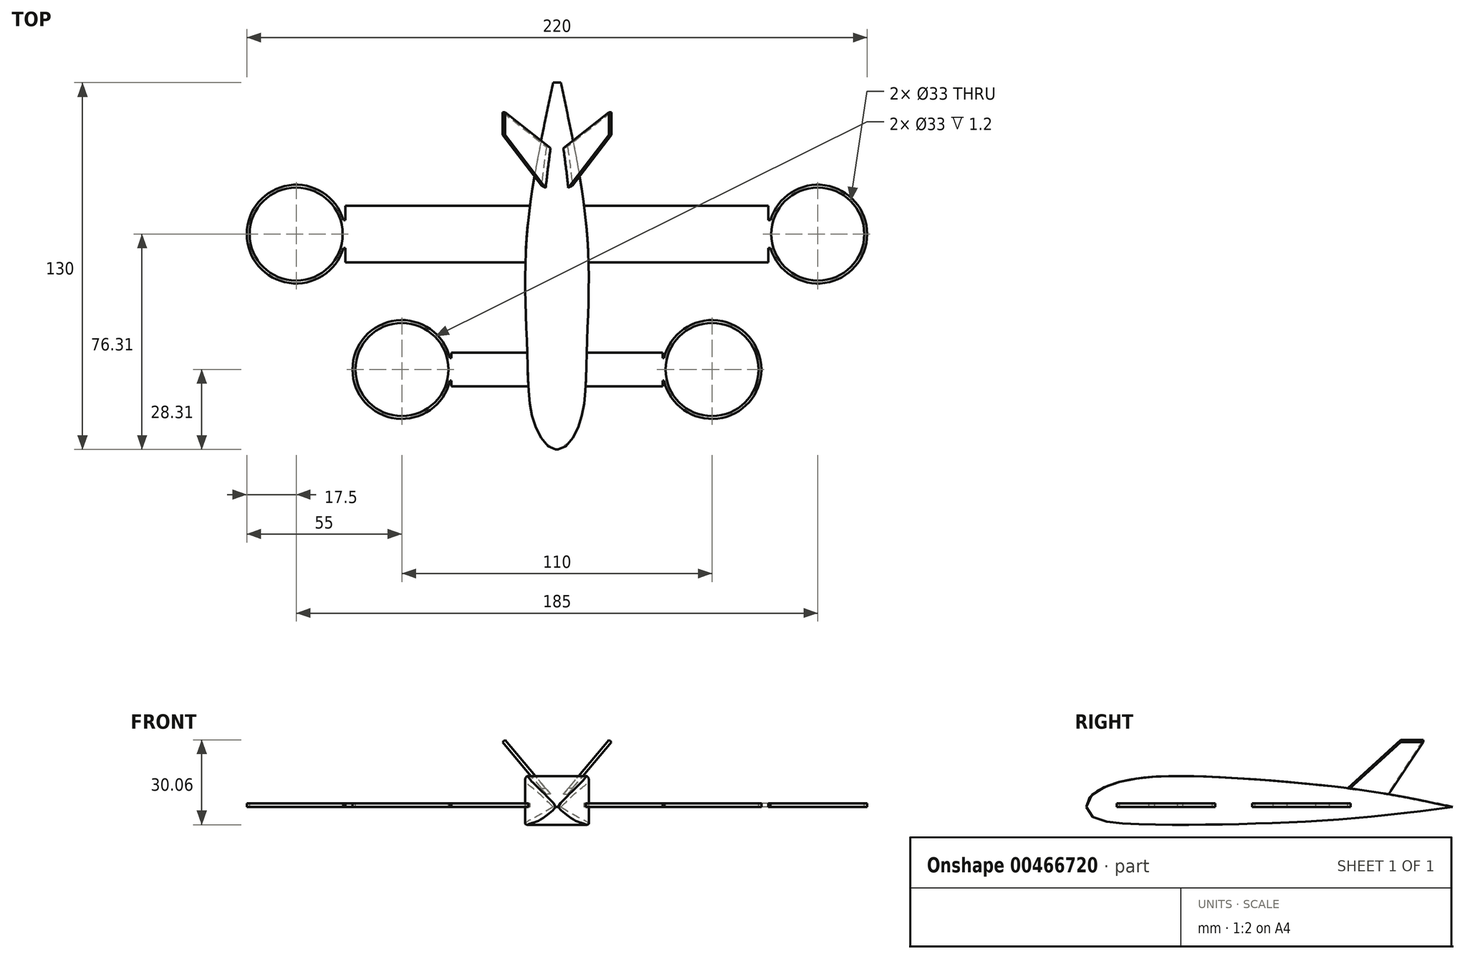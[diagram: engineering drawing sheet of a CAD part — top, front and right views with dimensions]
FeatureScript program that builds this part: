
annotation { "Feature Type Name" : "Feature", "Feature Type Description" : "" }
export const myFeature = defineFeature(function(context is Context, id is Id, definition is map)
    precondition{}
    {
        {
            var Q0;
            Q0=qCreatedBy(makeId("Right.planeOp"),FACE);
            var sketch = newSketch(context, id + "F0", { "sketchPlane" : qUnion([Q0])});
            skLineSegment(sketch, "E0", {"start": v(-56.31, 0) * mm, "end": v(73.69, 0) * mm, "construction": true});
            skFitSpline(sketch, "E1", {"points": [v(-56.31, 0) * mm, v(-53.08, 5.25) * mm, v(-41.18, 9.62) * mm, v(-16.4, 10.84) * mm, v(37.75, 6.46) * mm, v(62.27, 2.34) * mm, v(73.69, 0) * mm], "startDerivative": vector(0.47, 70.82) * mm, "endDerivative": vector(84.43, -17.46) * mm});
            skFitSpline(sketch, "E2", {"points": [v(-56.31, 0) * mm, v(-54.05, -3.5) * mm, v(-41.42, -5.92) * mm, v(25.6, -4.95) * mm, v(73.69, 0) * mm], "startDerivative": vector(0.9, -43.03) * mm, "endDerivative": vector(129.36, 17.02) * mm});
            skSolve(sketch);
        }
        {
            var Q0;
            Q0 = qSketchRegion(id + "F0", true);
            extrude(context, id + "F1", {"entities" : qUnion([Q0]), "endBound" : BoundingType.SYMMETRIC, "depth" : 25 * mm});
        }
        {
            var Q0;
            Q0=qCreatedBy(makeId("Top.planeOp"),FACE);
            var sketch = newSketch(context, id + "F2", { "sketchPlane" : qUnion([Q0])});
            skFitSpline(sketch, "E3", {"points": [v(0, -56.4) * mm, v(3.3, -55.05) * mm, v(8.09, -46.94) * mm, v(10.08, -35.65) * mm, v(10.66, -17.99) * mm, v(10.7, 19.52) * mm, v(1.38, 73.69) * mm], "startDerivative": vector(38.25, 6.4) * mm, "endDerivative": vector(-40.82, 194.33) * mm});
            skLineSegment(sketch, "E4", {"start": v(0, -56.4) * mm, "end": v(0, 73.69) * mm, "construction": true});
            skFitSpline(sketch, "E5.MirrorCS", {"points": [v(0, -56.4) * mm, v(-3.3, -55.05) * mm, v(-8.09, -46.94) * mm, v(-10.08, -35.65) * mm, v(-10.66, -17.99) * mm, v(-10.7, 19.52) * mm, v(-1.38, 73.69) * mm], "startDerivative": vector(-38.25, 6.4) * mm, "endDerivative": vector(40.82, 194.33) * mm});
            skLineSegment(sketch, "E6", {"start": v(-1.38, 73.69) * mm, "end": v(-1.38, 75.7) * mm});
            skLineSegment(sketch, "E7", {"start": v(-1.38, 75.7) * mm, "end": v(-14.03, 75.7) * mm});
            skLineSegment(sketch, "E8", {"start": v(-14.03, 75.7) * mm, "end": v(-14.03, -57.73) * mm});
            skLineSegment(sketch, "E9", {"start": v(-14.03, -57.73) * mm, "end": v(14.85, -57.73) * mm});
            skLineSegment(sketch, "E10", {"start": v(14.85, -57.73) * mm, "end": v(14.85, 75.71) * mm});
            skLineSegment(sketch, "E11", {"start": v(14.85, 75.71) * mm, "end": v(1.36, 75.71) * mm});
            skLineSegment(sketch, "E12", {"start": v(1.36, 75.71) * mm, "end": v(1.38, 73.69) * mm});
            skSolve(sketch);
        }
        {
            var Q0;
            Q0 = qSketchRegion(id + "F2", true);
            extrude(context, id + "F3", {"entities" : qUnion([Q0]), "operationType" : NewBodyOperationType.REMOVE, "endBound" : BoundingType.SYMMETRIC, "depth" : 100 * mm});
        }
        {
            var Q0;
            Q0=qCreatedBy(makeId("Right.planeOp"),FACE);
            var sketch = newSketch(context, id + "F4", { "sketchPlane" : qUnion([Q0])});
            skLineSegment(sketch, "E13.bottom", {"start": v(-34, 0) * mm, "end": v(-22, 0) * mm});
            skLineSegment(sketch, "E13.top", {"start": v(-34, 1.2) * mm, "end": v(-22, 1.2) * mm});
            skLineSegment(sketch, "E13.left", {"start": v(-34, 0) * mm, "end": v(-34, 1.2) * mm});
            skLineSegment(sketch, "E13.right", {"start": v(-22, 0) * mm, "end": v(-22, 1.2) * mm});
            skSolve(sketch);
        }
        {
            var Q0;
            Q0 = qSketchRegion(id + "F4", true);
            extrude(context, id + "F5", {"entities" : qUnion([Q0]), "operationType" : NewBodyOperationType.ADD, "endBound" : BoundingType.SYMMETRIC, "depth" : 75 * mm});
        }
        {
            var Q0;
            Q0=qCreatedBy(makeId("Right.planeOp"),FACE);
            var sketch = newSketch(context, id + "F6", { "sketchPlane" : qUnion([Q0])});
            skLineSegment(sketch, "E14.bottom", {"start": v(10, 0) * mm, "end": v(30, 0) * mm});
            skLineSegment(sketch, "E14.top", {"start": v(10, 1.2) * mm, "end": v(30, 1.2) * mm});
            skLineSegment(sketch, "E14.left", {"start": v(10, 0) * mm, "end": v(10, 1.2) * mm});
            skLineSegment(sketch, "E14.right", {"start": v(30, 0) * mm, "end": v(30, 1.2) * mm});
            skSolve(sketch);
        }
        {
            var Q0;
            Q0 = qSketchRegion(id + "F6", true);
            extrude(context, id + "F7", {"entities" : qUnion([Q0]), "operationType" : NewBodyOperationType.ADD, "endBound" : BoundingType.SYMMETRIC, "depth" : 150 * mm});
        }
        {
            var Q0;
            {var subQ2=sQuery(id+"F6.wireOp",EDGE,"E14.top");Q0=makeQuery(id+"F7.boolean.opBoolean","SPLIT",FACE,{"disambiguationData":[TD([makeQuery(id+"F3.boolean.opBoolean","COPY",FACE,{"derivedFrom":makeQuery(id+"F3.opExtrude","SWEPT_FACE",FACE,{"disambiguationData":[OSD([sQuery(id+"F2.wireOp",EDGE,"E3")])]})})])],"derivedFrom":makeQuery(id+"F7.opExtrude","SWEPT_FACE",FACE,{"disambiguationData":[OSD([subQ2])]})});}
            var sketch = newSketch(context, id + "F8", { "sketchPlane" : qUnion([Q0])});
            skArc(sketch, "E15", {"start": v(75.73, 15) * mm, "mid": v(110, 20) * mm, "end": v(75.73, 25) * mm});
            skLineSegment(sketch, "E16", {"start": v(92.5, 20) * mm, "end": v(75, 20) * mm, "construction": true});
            skPoint(sketch, "E16.endSnap0", {"position": v(75, 20) * mm});
            skLineSegment(sketch, "E17", {"start": v(75.73, 25) * mm, "end": v(73, 25) * mm});
            skLineSegment(sketch, "E18", {"start": v(73, 25) * mm, "end": v(73, 15) * mm});
            skLineSegment(sketch, "E19", {"start": v(73, 15) * mm, "end": v(75.73, 15) * mm});
            skCircle(sketch, "E20", {"center": v(92.5, 20) * mm, "radius": 16.5 * mm});
            skLineSegment(sketch, "E21", {"start": v(75, 20) * mm, "end": v(73, 20) * mm, "construction": true});
            skLineSegment(sketch, "E22", {"start": v(0, 0) * mm, "end": v(0, 50.66) * mm, "construction": true});
            skLineSegment(sketch, "E23.MirrorCS", {"start": v(-75, 20) * mm, "end": v(-73, 20) * mm, "construction": true});
            skLineSegment(sketch, "E24.MirrorCS", {"start": v(-73, 15) * mm, "end": v(-75.73, 15) * mm});
            skLineSegment(sketch, "E25.MirrorCS", {"start": v(-75.73, 25) * mm, "end": v(-73, 25) * mm});
            skLineSegment(sketch, "E26.MirrorCS", {"start": v(-73, 25) * mm, "end": v(-73, 15) * mm});
            skArc(sketch, "E27.MirrorCS", {"start": v(-75.73, 15) * mm, "mid": v(-110, 20) * mm, "end": v(-75.73, 25) * mm});
            skCircle(sketch, "E28.MirrorC", {"center": v(-92.5, 20) * mm, "radius": 16.5 * mm});
            skSolve(sketch);
        }
        {
            var Q0;
            Q0 = qSketchRegion(id + "F8", true);
            extrude(context, id + "F9", {"entities" : qUnion([Q0]), "operationType" : NewBodyOperationType.ADD, "oppositeDirection" : true, "depth" : 1.2 * mm});
        }
        {
            var Q0;
            {var subQ2=sQuery(id+"F4.wireOp",EDGE,"E13.top");Q0=makeQuery(id+"F5.boolean.opBoolean","SPLIT",FACE,{"disambiguationData":[TD([makeQuery(id+"F3.boolean.opBoolean","COPY",FACE,{"derivedFrom":makeQuery(id+"F3.opExtrude","SWEPT_FACE",FACE,{"disambiguationData":[OSD([sQuery(id+"F2.wireOp",EDGE,"E3")])]})})])],"derivedFrom":makeQuery(id+"F5.opExtrude","SWEPT_FACE",FACE,{"disambiguationData":[OSD([subQ2])]})});}
            var sketch = newSketch(context, id + "F10", { "sketchPlane" : qUnion([Q0])});
            skArc(sketch, "E29", {"start": v(37.96, -32) * mm, "mid": v(72.5, -28) * mm, "end": v(37.96, -24) * mm});
            skCircle(sketch, "E30", {"center": v(55, -28) * mm, "radius": 16.5 * mm});
            skLineSegment(sketch, "E31", {"start": v(55, -28) * mm, "end": v(37.5, -28) * mm, "construction": true});
            skLineSegment(sketch, "E32", {"start": v(37.96, -24) * mm, "end": v(35.5, -24) * mm});
            skLineSegment(sketch, "E33", {"start": v(35.5, -24) * mm, "end": v(35.5, -32) * mm});
            skLineSegment(sketch, "E34", {"start": v(35.5, -32) * mm, "end": v(37.96, -32) * mm});
            skLineSegment(sketch, "E35", {"start": v(37.5, -28) * mm, "end": v(35.5, -28) * mm, "construction": true});
            skLineSegment(sketch, "E36.MirrorCS", {"start": v(-35.5, -32) * mm, "end": v(-37.96, -32) * mm});
            skLineSegment(sketch, "E37.MirrorCS", {"start": v(-35.5, -24) * mm, "end": v(-35.5, -32) * mm});
            skLineSegment(sketch, "E38.MirrorCS", {"start": v(-37.96, -24) * mm, "end": v(-35.5, -24) * mm});
            skArc(sketch, "E39.MirrorCS", {"start": v(-37.96, -32) * mm, "mid": v(-72.5, -28) * mm, "end": v(-37.96, -24) * mm});
            skCircle(sketch, "E40.MirrorC", {"center": v(-55, -28) * mm, "radius": 16.5 * mm});
            skSolve(sketch);
        }
        {
            var Q0;
            Q0 = qSketchRegion(id + "F10", true);
            extrude(context, id + "F11", {"entities" : qUnion([Q0]), "operationType" : NewBodyOperationType.ADD, "oppositeDirection" : true, "depth" : 1.2 * mm});
        }
        {
            var Q0;
            Q0=qCreatedBy(makeId("Front.planeOp"),FACE);
            var sketch = newSketch(context, id + "F12", { "sketchPlane" : qUnion([Q0])});
            skLineSegment(sketch, "E41", {"start": v(0, 0) * mm, "end": v(34.79, 41.46) * mm, "construction": true});
            skSolve(sketch);
        }
        {
            var Q0;
            Q0=qCreatedBy(makeId("Right.planeOp"),FACE);
            var Q1;
            Q1=sQuery(id+"F12.wireOp",EDGE,"E41");
            cPlane(context, id + "F13", {"entities" : qUnion([Q0, Q1]), "cplaneType" : CPlaneType.LINE_ANGLE, "offset" : 25 * mm, "angle" : 0 * degree, "width" : 150 * mm, "height" : 150 * mm});
        }
        {
            var Q0;
            Q0=qCreatedBy(id+"F13.planeOp",FACE);
            var sketch = newSketch(context, id + "F14", { "sketchPlane" : qUnion([Q0])});
            skLineSegment(sketch, "E42", {"start": v(-30, 0) * mm, "end": v(-55.17, 30) * mm});
            skLineSegment(sketch, "E43", {"start": v(-55.17, 30) * mm, "end": v(-63.17, 30) * mm});
            skLineSegment(sketch, "E44", {"start": v(-63.17, 30) * mm, "end": v(-48, 0) * mm});
            skLineSegment(sketch, "E45", {"start": v(-48, 0) * mm, "end": v(-30, 0) * mm});
            skSolve(sketch);
        }
        {
            var Q0;
            Q0 = qSketchRegion(id + "F14", true);
            extrude(context, id + "F15", {"entities" : qUnion([Q0]), "operationType" : NewBodyOperationType.ADD, "depth" : 1.2 * mm});
        }
        {
            var Q0;
            Q0=makeQuery(id+"F1.opExtrude","SWEPT_BODY",BODY,{"disambiguationData":[OSD([sQuery(id+"F0.wireOp",EDGE,"E1"),sQuery(id+"F0.wireOp",EDGE,"E2")])]});
            var Q1;
            Q1=qCreatedBy(makeId("Right.planeOp"),FACE);
            mirror(context, id + "F16", {"operationType" : NewBodyOperationType.ADD, "entities" : qUnion([Q0]), "mirrorPlane" : qUnion([Q1])});
        }
    });
